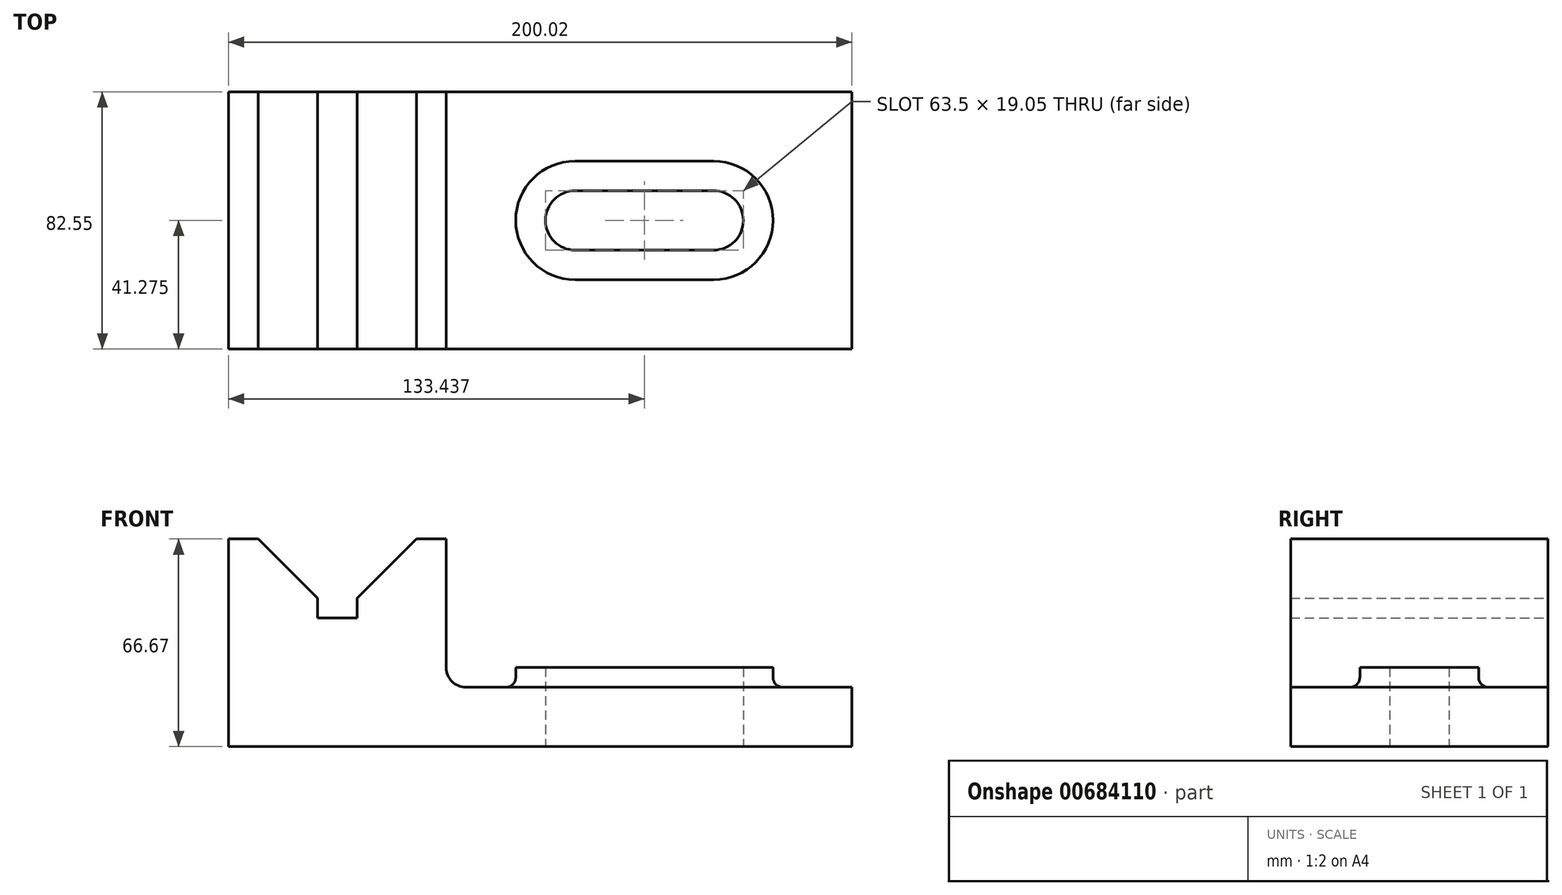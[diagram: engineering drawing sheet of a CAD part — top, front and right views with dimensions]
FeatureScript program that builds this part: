
annotation { "Feature Type Name" : "Feature", "Feature Type Description" : "" }
export const myFeature = defineFeature(function(context is Context, id is Id, definition is map)
    precondition{}
    {
        {
            var Q0;
            Q0=qCreatedBy(makeId("Front.planeOp"),FACE);
            var sketch = newSketch(context, id + "F0", { "sketchPlane" : qUnion([Q0])});
            skLineSegment(sketch, "E0", {"start": v(-63.55, 25.4) * mm, "end": v(-63.55, -41.28) * mm});
            skLineSegment(sketch, "E1", {"start": v(-63.55, -41.28) * mm, "end": v(136.47, -41.27) * mm});
            skLineSegment(sketch, "E2", {"start": v(136.47, -41.27) * mm, "end": v(136.47, -22.23) * mm});
            skLineSegment(sketch, "E3", {"start": v(136.47, -22.23) * mm, "end": v(12.65, -22.23) * mm});
            skLineSegment(sketch, "E4", {"start": v(6.3, -15.88) * mm, "end": v(6.3, 25.4) * mm});
            skLineSegment(sketch, "E5", {"start": v(-3.23, 25.4) * mm, "end": v(-22.28, 6.35) * mm});
            skLineSegment(sketch, "E6", {"start": v(-63.55, 25.4) * mm, "end": v(-54.03, 25.4) * mm});
            skLineSegment(sketch, "E7", {"start": v(-54.03, 25.4) * mm, "end": v(-34.98, 6.35) * mm});
            skLineSegment(sketch, "E8.trimOffspring", {"start": v(-54.03, 25.4) * mm, "end": v(-63.55, 25.4) * mm});
            skPoint(sketch, "E9.end.orphan", {"position": v(0, 23.13) * mm});
            skLineSegment(sketch, "E10", {"start": v(-3.23, 25.4) * mm, "end": v(6.3, 25.4) * mm});
            skPoint(sketch, "E11.visualSharp", {"position": v(6.3, -22.23) * mm});
            skArc(sketch, "E11.filletArc", {"start": v(6.3, -15.88) * mm, "mid": v(8.16, -20.37) * mm, "end": v(12.65, -22.23) * mm});
            skLineSegment(sketch, "E12", {"start": v(-34.98, 6.35) * mm, "end": v(-34.98, 0) * mm});
            skLineSegment(sketch, "E13", {"start": v(-34.98, 0) * mm, "end": v(-22.28, 0) * mm});
            skLineSegment(sketch, "E14", {"start": v(-22.28, 0) * mm, "end": v(-22.28, 6.35) * mm});
            skSolve(sketch);
        }
        {
            var Q0;
            Q0 = qSketchRegion(id + "F0", true);
            extrude(context, id + "F1", {"entities" : qUnion([Q0]), "depth" : 82.55 * mm, "offsetDistance" : 25.4 * mm});
        }
        {
            var Q0;
            Q0=makeQuery(id+"F1.opExtrude","SWEPT_FACE",FACE,{"disambiguationData":[OSD([sQuery(id+"F0.wireOp",EDGE,"E3")])]});
            var sketch = newSketch(context, id + "F2", { "sketchPlane" : qUnion([Q0])});
            skLineSegment(sketch, "E15.bottom", {"start": v(47.66, -50.8) * mm, "end": v(92.11, -50.8) * mm});
            skLineSegment(sketch, "E15.top", {"start": v(47.66, -31.75) * mm, "end": v(92.11, -31.75) * mm});
            skLineSegment(sketch, "E15.left", {"start": v(47.66, -50.8) * mm, "end": v(47.66, -31.75) * mm});
            skLineSegment(sketch, "E15.right", {"start": v(92.11, -50.8) * mm, "end": v(92.11, -31.75) * mm});
            skArc(sketch, "E16", {"start": v(47.66, -31.75) * mm, "mid": v(38.14, -41.28) * mm, "end": v(47.66, -50.8) * mm});
            skArc(sketch, "E17", {"start": v(92.11, -50.8) * mm, "mid": v(101.64, -41.28) * mm, "end": v(92.11, -31.75) * mm});
            skLineSegment(sketch, "E18.bottom", {"start": v(47.66, -60.33) * mm, "end": v(92.11, -60.33) * mm});
            skLineSegment(sketch, "E18.top", {"start": v(47.66, -22.23) * mm, "end": v(92.11, -22.23) * mm});
            skLineSegment(sketch, "E18.left", {"start": v(47.66, -60.33) * mm, "end": v(47.66, -22.23) * mm});
            skLineSegment(sketch, "E18.right", {"start": v(92.11, -60.33) * mm, "end": v(92.11, -22.23) * mm});
            skArc(sketch, "E19", {"start": v(47.66, -22.23) * mm, "mid": v(28.61, -41.28) * mm, "end": v(47.66, -60.33) * mm});
            skArc(sketch, "E20", {"start": v(92.11, -60.33) * mm, "mid": v(111.16, -41.28) * mm, "end": v(92.11, -22.23) * mm});
            skSolve(sketch);
        }
        {
            var Q0;
            {var subQ0=sQuery(id+"F2.wireOp",EDGE,"E16");Q0=makeQuery(id+"F2.imprint","IMPRINT",FACE,{"disambiguationData":[TD([[makeQuery(id+"F2.imprint","IMPRINT",EDGE,{"derivedFrom":subQ0}),-1.0]])]});}
            var Q1;
            {var subQ0=sQuery(id+"F2.wireOp",EDGE,"E15.bottom");Q1=makeQuery(id+"F2.imprint","IMPRINT",FACE,{"disambiguationData":[TD([[makeQuery(id+"F2.imprint","IMPRINT",EDGE,{"derivedFrom":subQ0}),-1.0]])]});}
            var Q2;
            {var subQ0=sQuery(id+"F2.wireOp",EDGE,"E17");Q2=makeQuery(id+"F2.imprint","IMPRINT",FACE,{"disambiguationData":[TD([[makeQuery(id+"F2.imprint","IMPRINT",EDGE,{"derivedFrom":subQ0}),-1.0]])]});}
            var Q3;
            {var subQ0=sQuery(id+"F2.wireOp",EDGE,"E15.top");Q3=makeQuery(id+"F2.imprint","IMPRINT",FACE,{"disambiguationData":[TD([[makeQuery(id+"F2.imprint","IMPRINT",EDGE,{"derivedFrom":subQ0}),1.0]])]});}
            extrude(context, id + "F3", {"entities" : qUnion([Q0, Q1, Q2, Q3]), "operationType" : NewBodyOperationType.ADD, "depth" : 6.35 * mm, "offsetDistance" : 25.4 * mm});
        }
        {
            var Q0;
            Q0=makeQuery(id+"F3.boolean.opBoolean","SPLIT",FACE,{"disambiguationData":[TD([makeQuery(id+"F3.opExtrude","SWEPT_FACE",FACE,{"disambiguationData":[OSD([sQuery(id+"F2.wireOp",EDGE,"E15.bottom")])]})])],"derivedFrom":makeQuery(id+"F1.opExtrude","SWEPT_FACE",FACE,{"disambiguationData":[OSD([sQuery(id+"F0.wireOp",EDGE,"E3")])]})});
            extrude(context, id + "F4", {"entities" : qUnion([Q0]), "operationType" : NewBodyOperationType.REMOVE, "oppositeDirection" : true, "depth" : 25.4 * mm, "offsetDistance" : 25.4 * mm});
        }
        {
            var Q0;
            Q0=makeQuery(id+"F3.opExtrude","CAP_EDGE",EDGE,{"disambiguationData":[OSD([sQuery(id+"F2.wireOp",EDGE,"E18.bottom")])],"isStart":true});
            fillet(context, id + "F5", {"entities" : qUnion([Q0]), "radius" : 3.17 * mm, "tangentPropagation" : true, "allowEdgeOverflow" : false});
        }
    });
